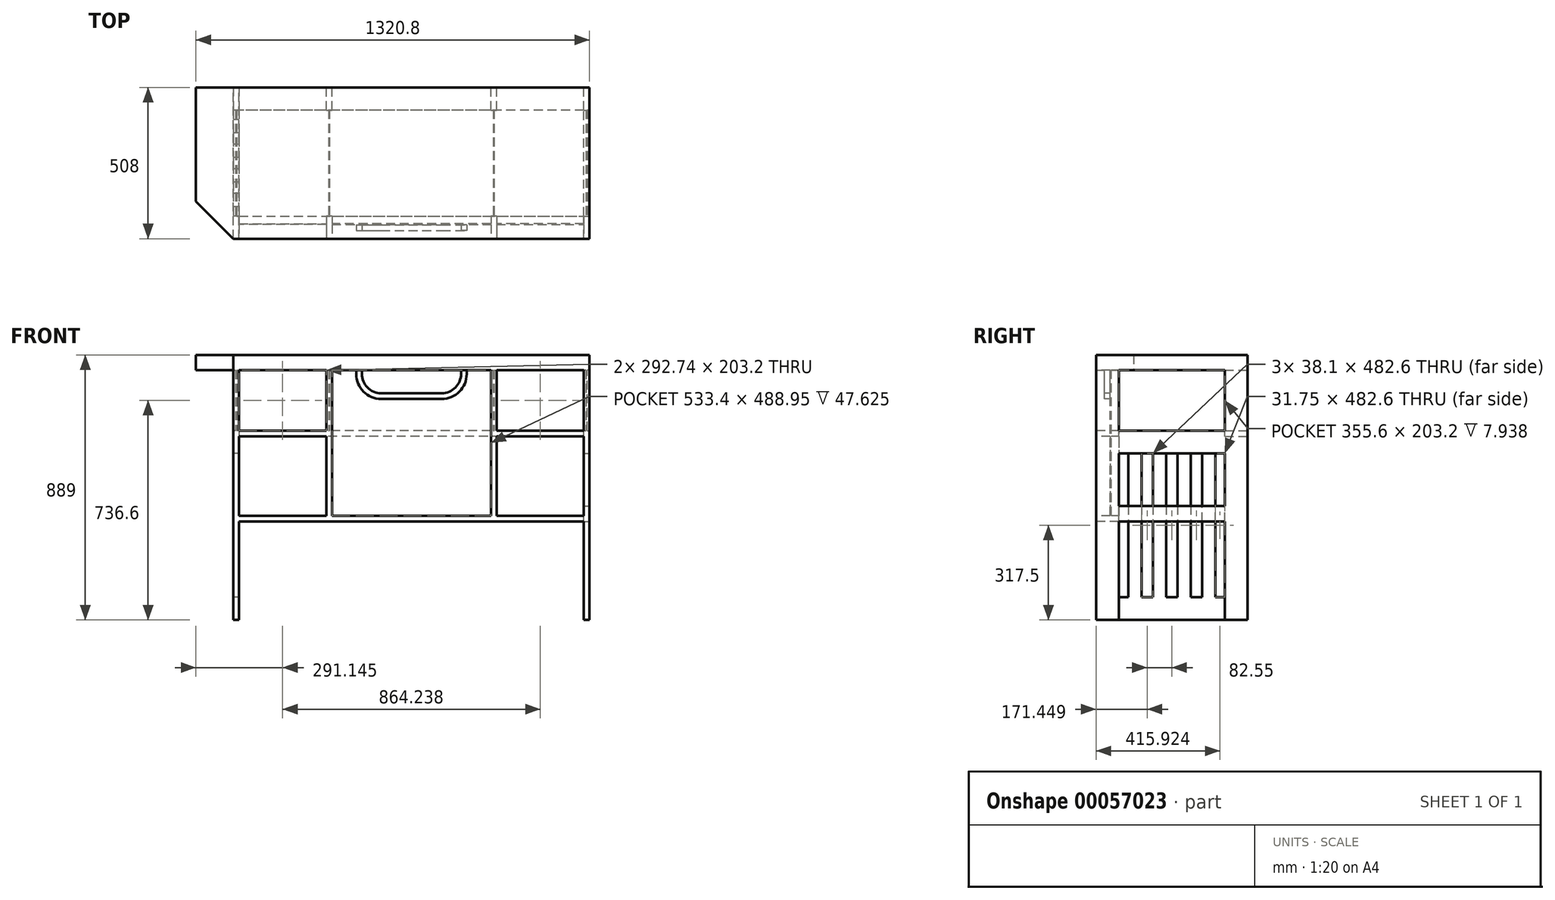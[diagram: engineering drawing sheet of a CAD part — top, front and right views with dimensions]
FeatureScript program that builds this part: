
annotation { "Feature Type Name" : "Feature", "Feature Type Description" : "" }
export const myFeature = defineFeature(function(context is Context, id is Id, definition is map)
    precondition{}
    {
        {
            var Q0;
            Q0=qCreatedBy(makeId("Top.planeOp"),FACE);
            var sketch = newSketch(context, id + "F0", { "sketchPlane" : qUnion([Q0])});
            skLineSegment(sketch, "E0", {"start": v(-703.39, 48.8) * mm, "end": v(617.41, 48.8) * mm});
            skLineSegment(sketch, "E1", {"start": v(617.41, 48.8) * mm, "end": v(617.41, -459.2) * mm});
            skLineSegment(sketch, "E2", {"start": v(617.41, -459.2) * mm, "end": v(-577.66, -459.2) * mm});
            skLineSegment(sketch, "E3", {"start": v(-577.66, -459.2) * mm, "end": v(-703.39, -333.48) * mm});
            skLineSegment(sketch, "E4", {"start": v(-703.39, -333.48) * mm, "end": v(-703.39, 48.8) * mm});
            skSolve(sketch);
        }
        {
            var Q0;
            Q0 = qSketchRegion(id + "F0", true);
            extrude(context, id + "F1", {"entities" : qUnion([Q0]), "depth" : 50.8 * mm});
        }
        {
            var Q0;
            Q0=makeQuery(id+"F1.opExtrude","CAP_FACE",FACE,{"disambiguationData":[OSD([sQuery(id+"F0.wireOp",EDGE,"E0"),sQuery(id+"F0.wireOp",EDGE,"E1"),sQuery(id+"F0.wireOp",EDGE,"E2"),sQuery(id+"F0.wireOp",EDGE,"E3"),sQuery(id+"F0.wireOp",EDGE,"E4")])],"isStart":true});
            var sketch = newSketch(context, id + "F2", { "sketchPlane" : qUnion([Q0])});
            skLineSegment(sketch, "E5.bottom", {"start": v(617.41, 459.2) * mm, "end": v(598.36, 459.2) * mm});
            skLineSegment(sketch, "E5.top", {"start": v(617.41, 383) * mm, "end": v(598.36, 383) * mm});
            skLineSegment(sketch, "E5.left", {"start": v(617.41, 459.2) * mm, "end": v(617.41, 383) * mm});
            skLineSegment(sketch, "E5.right", {"start": v(598.36, 459.2) * mm, "end": v(598.36, 383) * mm});
            skLineSegment(sketch, "E6.bottom", {"start": v(617.41, -48.8) * mm, "end": v(598.36, -48.8) * mm});
            skLineSegment(sketch, "E6.top", {"start": v(617.41, 27.4) * mm, "end": v(598.36, 27.4) * mm});
            skLineSegment(sketch, "E6.left", {"start": v(617.41, -48.8) * mm, "end": v(617.41, 27.4) * mm});
            skLineSegment(sketch, "E6.right", {"start": v(598.36, -48.8) * mm, "end": v(598.36, 27.4) * mm});
            skLineSegment(sketch, "E7.bottom", {"start": v(-577.66, 459.2) * mm, "end": v(-558.61, 459.2) * mm});
            skLineSegment(sketch, "E7.top", {"start": v(-577.66, 383) * mm, "end": v(-558.61, 383) * mm});
            skLineSegment(sketch, "E7.left", {"start": v(-577.66, 459.2) * mm, "end": v(-577.66, 383) * mm});
            skLineSegment(sketch, "E7.right", {"start": v(-558.61, 459.2) * mm, "end": v(-558.61, 383) * mm});
            skLineSegment(sketch, "E8.bottom", {"start": v(-577.66, -48.8) * mm, "end": v(-558.61, -48.8) * mm});
            skLineSegment(sketch, "E8.top", {"start": v(-577.66, 27.4) * mm, "end": v(-558.61, 27.4) * mm});
            skLineSegment(sketch, "E8.left", {"start": v(-577.66, -48.8) * mm, "end": v(-577.66, 27.4) * mm});
            skLineSegment(sketch, "E8.right", {"start": v(-558.61, -48.8) * mm, "end": v(-558.61, 27.4) * mm});
            skSolve(sketch);
        }
        {
            var Q0;
            Q0 = qSketchRegion(id + "F2", true);
            extrude(context, id + "F3", {"entities" : qUnion([Q0]), "operationType" : NewBodyOperationType.ADD, "depth" : 838.2 * mm});
        }
        {
            var Q0;
            Q0=makeQuery(id+"F3.opExtrude","SWEPT_FACE",FACE,{"disambiguationData":[OSD([sQuery(id+"F2.wireOp",EDGE,"E8.left")])]});
            var sketch = newSketch(context, id + "F4", { "sketchPlane" : qUnion([Q0])});
            skLineSegment(sketch, "E9.bottom", {"start": v(27.4, -203.2) * mm, "end": v(383, -203.2) * mm});
            skLineSegment(sketch, "E9.top", {"start": v(27.4, -279.4) * mm, "end": v(383, -279.4) * mm});
            skLineSegment(sketch, "E9.left", {"start": v(27.4, -203.2) * mm, "end": v(27.4, -279.4) * mm});
            skLineSegment(sketch, "E9.right", {"start": v(383, -203.2) * mm, "end": v(383, -279.4) * mm});
            skLineSegment(sketch, "E10.bottom", {"start": v(27.4, -838.2) * mm, "end": v(383, -838.2) * mm});
            skLineSegment(sketch, "E10.top", {"start": v(27.4, -762) * mm, "end": v(383, -762) * mm});
            skLineSegment(sketch, "E10.left", {"start": v(27.4, -838.2) * mm, "end": v(27.4, -762) * mm});
            skLineSegment(sketch, "E10.right", {"start": v(383, -838.2) * mm, "end": v(383, -762) * mm});
            skSolve(sketch);
        }
        {
            var Q0;
            Q0 = qSketchRegion(id + "F4", true);
            extrude(context, id + "F5", {"entities" : qUnion([Q0]), "operationType" : NewBodyOperationType.ADD, "oppositeDirection" : true, "depth" : 19.05 * mm});
        }
        {
            var Q0;
            Q0=makeQuery(id+"F5.boolean.opBoolean","MERGE",FACE,{"derivedFrom":[makeQuery(id+"F3.opExtrude","SWEPT_FACE",FACE,{"disambiguationData":[OSD([sQuery(id+"F2.wireOp",EDGE,"E7.left")])]}),makeQuery(id+"F3.opExtrude","SWEPT_FACE",FACE,{"disambiguationData":[OSD([sQuery(id+"F2.wireOp",EDGE,"E8.left")])]}),makeQuery(id+"F5.opExtrude","CAP_FACE",FACE,{"disambiguationData":[OSD([sQuery(id+"F4.wireOp",EDGE,"E9.bottom"),sQuery(id+"F4.wireOp",EDGE,"E9.top"),sQuery(id+"F4.wireOp",EDGE,"E9.left"),sQuery(id+"F4.wireOp",EDGE,"E9.right")])],"isStart":true}),makeQuery(id+"F5.opExtrude","CAP_FACE",FACE,{"disambiguationData":[OSD([sQuery(id+"F4.wireOp",EDGE,"E10.bottom"),sQuery(id+"F4.wireOp",EDGE,"E10.top"),sQuery(id+"F4.wireOp",EDGE,"E10.left"),sQuery(id+"F4.wireOp",EDGE,"E10.right")])],"isStart":true})]});
            var sketch = newSketch(context, id + "F6", { "sketchPlane" : qUnion([Q0])});
            skLineSegment(sketch, "E11.bottom", {"start": v(59.15, -762) * mm, "end": v(103.6, -762) * mm});
            skLineSegment(sketch, "E11.top", {"start": v(59.15, -279.4) * mm, "end": v(103.6, -279.4) * mm});
            skLineSegment(sketch, "E11.left", {"start": v(59.15, -762) * mm, "end": v(59.15, -279.4) * mm});
            skLineSegment(sketch, "E11.right", {"start": v(103.6, -762) * mm, "end": v(103.6, -279.4) * mm});
            skLineSegment(sketch, "E12.top", {"start": v(141.7, -762) * mm, "end": v(186.15, -762) * mm});
            skLineSegment(sketch, "E12.left", {"start": v(141.7, -279.4) * mm, "end": v(141.7, -762) * mm});
            skLineSegment(sketch, "E12.right", {"start": v(186.15, -279.4) * mm, "end": v(186.15, -762) * mm});
            skLineSegment(sketch, "E13.bottom", {"start": v(224.25, -279.4) * mm, "end": v(268.7, -279.4) * mm});
            skLineSegment(sketch, "E13.top", {"start": v(224.25, -762) * mm, "end": v(268.7, -762) * mm});
            skLineSegment(sketch, "E13.left", {"start": v(224.25, -279.4) * mm, "end": v(224.25, -762) * mm});
            skLineSegment(sketch, "E13.right", {"start": v(268.7, -279.4) * mm, "end": v(268.7, -762) * mm});
            skLineSegment(sketch, "E14.bottom", {"start": v(306.8, -279.4) * mm, "end": v(351.25, -279.4) * mm});
            skLineSegment(sketch, "E14.top", {"start": v(306.8, -762) * mm, "end": v(351.25, -762) * mm});
            skLineSegment(sketch, "E14.left", {"start": v(306.8, -279.4) * mm, "end": v(306.8, -762) * mm});
            skLineSegment(sketch, "E14.right", {"start": v(351.25, -279.4) * mm, "end": v(351.25, -762) * mm});
            skLineSegment(sketch, "E15", {"start": v(103.6, -279.4) * mm, "end": v(141.7, -279.4) * mm, "construction": true});
            skLineSegment(sketch, "E16", {"start": v(141.7, -279.4) * mm, "end": v(186.15, -279.4) * mm});
            skSolve(sketch);
        }
        {
            var Q0;
            Q0 = qSketchRegion(id + "F6", true);
            var Q1;
            Q1=makeQuery(id+"F5.boolean.opBoolean","MERGE",FACE,{"derivedFrom":[makeQuery(id+"F3.opExtrude","SWEPT_FACE",FACE,{"disambiguationData":[OSD([sQuery(id+"F2.wireOp",EDGE,"E7.right")])]}),makeQuery(id+"F3.opExtrude","SWEPT_FACE",FACE,{"disambiguationData":[OSD([sQuery(id+"F2.wireOp",EDGE,"E8.right")])]}),makeQuery(id+"F5.opExtrude","CAP_FACE",FACE,{"disambiguationData":[OSD([sQuery(id+"F4.wireOp",EDGE,"E9.bottom"),sQuery(id+"F4.wireOp",EDGE,"E9.top"),sQuery(id+"F4.wireOp",EDGE,"E9.left"),sQuery(id+"F4.wireOp",EDGE,"E9.right")])],"isStart":false}),makeQuery(id+"F5.opExtrude","CAP_FACE",FACE,{"disambiguationData":[OSD([sQuery(id+"F4.wireOp",EDGE,"E10.bottom"),sQuery(id+"F4.wireOp",EDGE,"E10.top"),sQuery(id+"F4.wireOp",EDGE,"E10.left"),sQuery(id+"F4.wireOp",EDGE,"E10.right")])],"isStart":false})]});
            extrude(context, id + "F7", {"entities" : qUnion([Q0]), "operationType" : NewBodyOperationType.ADD, "endBound" : BoundingType.UP_TO_SURFACE, "oppositeDirection" : true, "endBoundEntityFace" : qUnion([Q1]), "depth" : 25.4 * mm});
        }
        {
            var Q0;
            Q0=makeQuery(id+"F3.boolean.opBoolean","MERGE",FACE,{"derivedFrom":[makeQuery(id+"F1.opExtrude","SWEPT_FACE",FACE,{"disambiguationData":[OSD([sQuery(id+"F0.wireOp",EDGE,"E2")])]}),makeQuery(id+"F3.opExtrude","SWEPT_FACE",FACE,{"disambiguationData":[OSD([sQuery(id+"F2.wireOp",EDGE,"E5.bottom")])]}),makeQuery(id+"F3.opExtrude","SWEPT_FACE",FACE,{"disambiguationData":[OSD([sQuery(id+"F2.wireOp",EDGE,"E7.bottom")])]})]});
            var sketch = newSketch(context, id + "F8", { "sketchPlane" : qUnion([Q0])});
            skLineSegment(sketch, "E17.bottom", {"start": v(-265.88, 0) * mm, "end": v(-246.83, 0) * mm});
            skLineSegment(sketch, "E17.top", {"start": v(-265.88, -222.25) * mm, "end": v(-246.83, -222.25) * mm});
            skLineSegment(sketch, "E17.left", {"start": v(-265.88, 0) * mm, "end": v(-265.88, -222.25) * mm});
            skLineSegment(sketch, "E17.right", {"start": v(-246.83, 0) * mm, "end": v(-246.83, -222.25) * mm});
            skLineSegment(sketch, "E18.bottom", {"start": v(286.57, 0) * mm, "end": v(305.62, 0) * mm});
            skLineSegment(sketch, "E18.top", {"start": v(286.57, -222.25) * mm, "end": v(305.62, -222.25) * mm});
            skLineSegment(sketch, "E18.left", {"start": v(286.57, 0) * mm, "end": v(286.57, -222.25) * mm});
            skLineSegment(sketch, "E18.right", {"start": v(305.62, 0) * mm, "end": v(305.62, -222.25) * mm});
            skLineSegment(sketch, "E19", {"start": v(-265.88, 0) * mm, "end": v(-558.61, 0) * mm});
            skLineSegment(sketch, "E20", {"start": v(305.62, 0) * mm, "end": v(598.36, 0) * mm});
            skLineSegment(sketch, "E21.bottom", {"start": v(-265.88, -222.25) * mm, "end": v(-558.61, -222.25) * mm});
            skLineSegment(sketch, "E21.top", {"start": v(-265.88, -203.2) * mm, "end": v(-558.61, -203.2) * mm});
            skLineSegment(sketch, "E21.left", {"start": v(-265.88, -222.25) * mm, "end": v(-265.88, -203.2) * mm});
            skLineSegment(sketch, "E21.right", {"start": v(-558.61, -222.25) * mm, "end": v(-558.61, -203.2) * mm});
            skLineSegment(sketch, "E22.bottom", {"start": v(305.62, -222.25) * mm, "end": v(598.36, -222.25) * mm});
            skLineSegment(sketch, "E22.top", {"start": v(305.62, -203.2) * mm, "end": v(598.36, -203.2) * mm});
            skLineSegment(sketch, "E22.left", {"start": v(305.62, -222.25) * mm, "end": v(305.62, -203.2) * mm});
            skLineSegment(sketch, "E22.right", {"start": v(598.36, -222.25) * mm, "end": v(598.36, -203.2) * mm});
            skSolve(sketch);
        }
        {
            var Q0;
            Q0=makeQuery(id+"F7.boolean.opBoolean","MERGE",FACE,{"derivedFrom":[makeQuery(id+"F5.boolean.opBoolean","MERGE",FACE,{"derivedFrom":[makeQuery(id+"F3.opExtrude","SWEPT_FACE",FACE,{"disambiguationData":[OSD([sQuery(id+"F2.wireOp",EDGE,"E7.right")])]}),makeQuery(id+"F3.opExtrude","SWEPT_FACE",FACE,{"disambiguationData":[OSD([sQuery(id+"F2.wireOp",EDGE,"E8.right")])]}),makeQuery(id+"F5.opExtrude","CAP_FACE",FACE,{"disambiguationData":[OSD([sQuery(id+"F4.wireOp",EDGE,"E9.bottom"),sQuery(id+"F4.wireOp",EDGE,"E9.top"),sQuery(id+"F4.wireOp",EDGE,"E9.left"),sQuery(id+"F4.wireOp",EDGE,"E9.right")])],"isStart":false}),makeQuery(id+"F5.opExtrude","CAP_FACE",FACE,{"disambiguationData":[OSD([sQuery(id+"F4.wireOp",EDGE,"E10.bottom"),sQuery(id+"F4.wireOp",EDGE,"E10.top"),sQuery(id+"F4.wireOp",EDGE,"E10.left"),sQuery(id+"F4.wireOp",EDGE,"E10.right")])],"isStart":false})]}),makeQuery(id+"F7.opExtrude","CAP_FACE",FACE,{"disambiguationData":[OSD([sQuery(id+"F6.wireOp",EDGE,"E11.bottom"),sQuery(id+"F6.wireOp",EDGE,"E11.top"),sQuery(id+"F6.wireOp",EDGE,"E11.left"),sQuery(id+"F6.wireOp",EDGE,"E11.right")])],"isStart":false}),makeQuery(id+"F7.opExtrude","CAP_FACE",FACE,{"disambiguationData":[OSD([sQuery(id+"F6.wireOp",EDGE,"E12.top"),sQuery(id+"F6.wireOp",EDGE,"E12.left"),sQuery(id+"F6.wireOp",EDGE,"E12.right"),sQuery(id+"F6.wireOp",EDGE,"E16")])],"isStart":false}),makeQuery(id+"F7.opExtrude","CAP_FACE",FACE,{"disambiguationData":[OSD([sQuery(id+"F6.wireOp",EDGE,"E13.bottom"),sQuery(id+"F6.wireOp",EDGE,"E13.top"),sQuery(id+"F6.wireOp",EDGE,"E13.left"),sQuery(id+"F6.wireOp",EDGE,"E13.right")])],"isStart":false}),makeQuery(id+"F7.opExtrude","CAP_FACE",FACE,{"disambiguationData":[OSD([sQuery(id+"F6.wireOp",EDGE,"E14.bottom"),sQuery(id+"F6.wireOp",EDGE,"E14.top"),sQuery(id+"F6.wireOp",EDGE,"E14.left"),sQuery(id+"F6.wireOp",EDGE,"E14.right")])],"isStart":false})]});
            var sketch = newSketch(context, id + "F9", { "sketchPlane" : qUnion([Q0])});
            skLineSegment(sketch, "E23.bottom", {"start": v(-27.4, -203.2) * mm, "end": v(48.8, -203.2) * mm});
            skLineSegment(sketch, "E23.top", {"start": v(-27.4, -222.25) * mm, "end": v(48.8, -222.25) * mm});
            skLineSegment(sketch, "E23.left", {"start": v(-27.4, -203.2) * mm, "end": v(-27.4, -222.25) * mm});
            skLineSegment(sketch, "E23.right", {"start": v(48.8, -203.2) * mm, "end": v(48.8, -222.25) * mm});
            skSolve(sketch);
        }
        {
            var Q0;
            Q0 = qSketchRegion(id + "F9", true);
            var Q1;
            Q1=makeQuery(id+"F3.opExtrude","SWEPT_FACE",FACE,{"disambiguationData":[OSD([sQuery(id+"F2.wireOp",EDGE,"E5.right")])]});
            extrude(context, id + "F10", {"entities" : qUnion([Q0]), "operationType" : NewBodyOperationType.ADD, "endBound" : BoundingType.UP_TO_SURFACE, "endBoundEntityFace" : qUnion([Q1]), "depth" : 25.4 * mm});
        }
        {
            var Q0;
            Q0 = qSketchRegion(id + "F8", true);
            extrude(context, id + "F11", {"entities" : qUnion([Q0]), "operationType" : NewBodyOperationType.ADD, "oppositeDirection" : true, "depth" : 76.2 * mm});
        }
        {
            var Q0;
            Q0=makeQuery(id+"F10.boolean.opBoolean","MERGE",FACE,{"derivedFrom":[makeQuery(id+"F3.boolean.opBoolean","MERGE",FACE,{"derivedFrom":[makeQuery(id+"F1.opExtrude","SWEPT_FACE",FACE,{"disambiguationData":[OSD([sQuery(id+"F0.wireOp",EDGE,"E0")])]}),makeQuery(id+"F3.opExtrude","SWEPT_FACE",FACE,{"disambiguationData":[OSD([sQuery(id+"F2.wireOp",EDGE,"E6.bottom")])]}),makeQuery(id+"F3.opExtrude","SWEPT_FACE",FACE,{"disambiguationData":[OSD([sQuery(id+"F2.wireOp",EDGE,"E8.bottom")])]})]}),makeQuery(id+"F10.opExtrude","SWEPT_FACE",FACE,{"disambiguationData":[OSD([sQuery(id+"F9.wireOp",EDGE,"E23.right")])]})]});
            var sketch = newSketch(context, id + "F12", { "sketchPlane" : qUnion([Q0])});
            skLineSegment(sketch, "E24.bottom", {"start": v(-305.62, 0) * mm, "end": v(-286.57, 0) * mm});
            skLineSegment(sketch, "E24.top", {"start": v(-305.62, -203.2) * mm, "end": v(-286.57, -203.2) * mm});
            skLineSegment(sketch, "E24.left", {"start": v(-305.62, 0) * mm, "end": v(-305.62, -203.2) * mm});
            skLineSegment(sketch, "E24.right", {"start": v(-286.57, 0) * mm, "end": v(-286.57, -203.2) * mm});
            skLineSegment(sketch, "E25.bottom", {"start": v(246.83, 0) * mm, "end": v(265.88, 0) * mm});
            skLineSegment(sketch, "E25.top", {"start": v(246.83, -203.2) * mm, "end": v(265.88, -203.2) * mm});
            skLineSegment(sketch, "E25.left", {"start": v(246.83, 0) * mm, "end": v(246.83, -203.2) * mm});
            skLineSegment(sketch, "E25.right", {"start": v(265.88, 0) * mm, "end": v(265.88, -203.2) * mm});
            skSolve(sketch);
        }
        {
            var Q0;
            Q0 = qSketchRegion(id + "F12", true);
            extrude(context, id + "F13", {"entities" : qUnion([Q0]), "operationType" : NewBodyOperationType.ADD, "oppositeDirection" : true, "depth" : 76.2 * mm});
        }
        {
            var Q0;
            Q0=makeQuery(id+"F11.boolean.opBoolean","MERGE",FACE,{"derivedFrom":[makeQuery(id+"F3.boolean.opBoolean","MERGE",FACE,{"derivedFrom":[makeQuery(id+"F1.opExtrude","SWEPT_FACE",FACE,{"disambiguationData":[OSD([sQuery(id+"F0.wireOp",EDGE,"E2")])]}),makeQuery(id+"F3.opExtrude","SWEPT_FACE",FACE,{"disambiguationData":[OSD([sQuery(id+"F2.wireOp",EDGE,"E5.bottom")])]}),makeQuery(id+"F3.opExtrude","SWEPT_FACE",FACE,{"disambiguationData":[OSD([sQuery(id+"F2.wireOp",EDGE,"E7.bottom")])]})]}),makeQuery(id+"F11.opExtrude","CAP_FACE",FACE,{"disambiguationData":[OSD([sQuery(id+"F8.wireOp",EDGE,"E17.bottom"),sQuery(id+"F8.wireOp",EDGE,"E17.top"),sQuery(id+"F8.wireOp",EDGE,"E17.left"),sQuery(id+"F8.wireOp",EDGE,"E17.right"),sQuery(id+"F8.wireOp",EDGE,"E21.bottom"),sQuery(id+"F8.wireOp",EDGE,"E21.top"),sQuery(id+"F8.wireOp",EDGE,"E21.right")])],"isStart":true}),makeQuery(id+"F11.opExtrude","CAP_FACE",FACE,{"disambiguationData":[OSD([sQuery(id+"F8.wireOp",EDGE,"E18.bottom"),sQuery(id+"F8.wireOp",EDGE,"E18.top"),sQuery(id+"F8.wireOp",EDGE,"E18.left"),sQuery(id+"F8.wireOp",EDGE,"E18.right"),sQuery(id+"F8.wireOp",EDGE,"E22.bottom"),sQuery(id+"F8.wireOp",EDGE,"E22.top"),sQuery(id+"F8.wireOp",EDGE,"E22.right")])],"isStart":true})]});
            var sketch = newSketch(context, id + "F14", { "sketchPlane" : qUnion([Q0])});
            skLineSegment(sketch, "E26.bottom", {"start": v(-569.73, 0) * mm, "end": v(-566.55, 0) * mm});
            skLineSegment(sketch, "E26.top", {"start": v(-569.73, -203.2) * mm, "end": v(-566.55, -203.2) * mm});
            skLineSegment(sketch, "E26.left", {"start": v(-569.73, 0) * mm, "end": v(-569.73, -203.2) * mm});
            skLineSegment(sketch, "E26.right", {"start": v(-566.55, 0) * mm, "end": v(-566.55, -203.2) * mm});
            skLineSegment(sketch, "E27.bottom", {"start": v(-257.97, 0) * mm, "end": v(-254.8, 0) * mm});
            skLineSegment(sketch, "E27.top", {"start": v(-257.97, -203.2) * mm, "end": v(-254.8, -203.2) * mm});
            skLineSegment(sketch, "E27.left", {"start": v(-257.97, 0) * mm, "end": v(-257.97, -203.2) * mm});
            skLineSegment(sketch, "E27.right", {"start": v(-254.8, 0) * mm, "end": v(-254.8, -203.2) * mm});
            skLineSegment(sketch, "E28.bottom", {"start": v(294.51, 0) * mm, "end": v(297.69, 0) * mm});
            skLineSegment(sketch, "E28.top", {"start": v(294.51, -203.2) * mm, "end": v(297.69, -203.2) * mm});
            skLineSegment(sketch, "E28.left", {"start": v(294.51, 0) * mm, "end": v(294.51, -203.2) * mm});
            skLineSegment(sketch, "E28.right", {"start": v(297.69, 0) * mm, "end": v(297.69, -203.2) * mm});
            skLineSegment(sketch, "E29.bottom", {"start": v(606.3, 0) * mm, "end": v(609.48, 0) * mm});
            skLineSegment(sketch, "E29.top", {"start": v(606.3, -203.2) * mm, "end": v(609.48, -203.2) * mm});
            skLineSegment(sketch, "E29.left", {"start": v(606.3, 0) * mm, "end": v(606.3, -203.2) * mm});
            skLineSegment(sketch, "E29.right", {"start": v(609.48, 0) * mm, "end": v(609.48, -203.2) * mm});
            skSolve(sketch);
        }
        {
            var Q0;
            Q0 = qSketchRegion(id + "F14", true);
            var Q1;
            Q1=makeQuery(id+"F13.boolean.opBoolean","MERGE",FACE,{"derivedFrom":[makeQuery(id+"F10.boolean.opBoolean","MERGE",FACE,{"derivedFrom":[makeQuery(id+"F3.opExtrude","SWEPT_FACE",FACE,{"disambiguationData":[OSD([sQuery(id+"F2.wireOp",EDGE,"E6.top")])]}),makeQuery(id+"F10.opExtrude","SWEPT_FACE",FACE,{"disambiguationData":[OSD([sQuery(id+"F9.wireOp",EDGE,"E23.left")])]})]}),makeQuery(id+"F13.opExtrude","CAP_FACE",FACE,{"disambiguationData":[OSD([sQuery(id+"F12.wireOp",EDGE,"E24.bottom"),sQuery(id+"F12.wireOp",EDGE,"E24.top"),sQuery(id+"F12.wireOp",EDGE,"E24.left"),sQuery(id+"F12.wireOp",EDGE,"E24.right")])],"isStart":false}),makeQuery(id+"F13.opExtrude","CAP_FACE",FACE,{"disambiguationData":[OSD([sQuery(id+"F12.wireOp",EDGE,"E25.bottom"),sQuery(id+"F12.wireOp",EDGE,"E25.top"),sQuery(id+"F12.wireOp",EDGE,"E25.left"),sQuery(id+"F12.wireOp",EDGE,"E25.right")])],"isStart":false})]});
            extrude(context, id + "F15", {"entities" : qUnion([Q0]), "operationType" : NewBodyOperationType.ADD, "endBound" : BoundingType.UP_TO_SURFACE, "oppositeDirection" : true, "endBoundEntityFace" : qUnion([Q1]), "depth" : 25.4 * mm});
        }
        {
            var Q0;
            Q0=makeQuery(id+"F3.boolean.opBoolean","MERGE",FACE,{"derivedFrom":[makeQuery(id+"F1.opExtrude","SWEPT_FACE",FACE,{"disambiguationData":[OSD([sQuery(id+"F0.wireOp",EDGE,"E1")])]}),makeQuery(id+"F3.opExtrude","SWEPT_FACE",FACE,{"disambiguationData":[OSD([sQuery(id+"F2.wireOp",EDGE,"E5.left")])]}),makeQuery(id+"F3.opExtrude","SWEPT_FACE",FACE,{"disambiguationData":[OSD([sQuery(id+"F2.wireOp",EDGE,"E6.left")])]})]});
            var sketch = newSketch(context, id + "F16", { "sketchPlane" : qUnion([Q0])});
            skLineSegment(sketch, "E30.bottom", {"start": v(-383, -203.2) * mm, "end": v(-27.4, -203.2) * mm});
            skLineSegment(sketch, "E30.top", {"start": v(-383, -279.4) * mm, "end": v(-27.4, -279.4) * mm});
            skLineSegment(sketch, "E30.left", {"start": v(-383, -203.2) * mm, "end": v(-383, -279.4) * mm});
            skLineSegment(sketch, "E30.right", {"start": v(-27.4, -203.2) * mm, "end": v(-27.4, -279.4) * mm});
            skLineSegment(sketch, "E31.bottom", {"start": v(-27.4, -508) * mm, "end": v(-383, -508) * mm});
            skLineSegment(sketch, "E31.top", {"start": v(-27.4, -455.56) * mm, "end": v(-383, -455.56) * mm});
            skLineSegment(sketch, "E31.left", {"start": v(-27.4, -508) * mm, "end": v(-27.4, -455.56) * mm});
            skLineSegment(sketch, "E31.right", {"start": v(-383, -508) * mm, "end": v(-383, -455.56) * mm});
            skSolve(sketch);
        }
        {
            var Q0;
            Q0 = qSketchRegion(id + "F16", true);
            extrude(context, id + "F17", {"entities" : qUnion([Q0]), "operationType" : NewBodyOperationType.ADD, "oppositeDirection" : true, "depth" : 19.05 * mm});
        }
        {
            var Q0;
            Q0=makeQuery(id+"F11.boolean.opBoolean","MERGE",FACE,{"derivedFrom":[makeQuery(id+"F3.boolean.opBoolean","MERGE",FACE,{"derivedFrom":[makeQuery(id+"F1.opExtrude","SWEPT_FACE",FACE,{"disambiguationData":[OSD([sQuery(id+"F0.wireOp",EDGE,"E2")])]}),makeQuery(id+"F3.opExtrude","SWEPT_FACE",FACE,{"disambiguationData":[OSD([sQuery(id+"F2.wireOp",EDGE,"E5.bottom")])]}),makeQuery(id+"F3.opExtrude","SWEPT_FACE",FACE,{"disambiguationData":[OSD([sQuery(id+"F2.wireOp",EDGE,"E7.bottom")])]})]}),makeQuery(id+"F11.opExtrude","CAP_FACE",FACE,{"disambiguationData":[OSD([sQuery(id+"F8.wireOp",EDGE,"E17.bottom"),sQuery(id+"F8.wireOp",EDGE,"E17.top"),sQuery(id+"F8.wireOp",EDGE,"E17.left"),sQuery(id+"F8.wireOp",EDGE,"E17.right"),sQuery(id+"F8.wireOp",EDGE,"E21.bottom"),sQuery(id+"F8.wireOp",EDGE,"E21.top"),sQuery(id+"F8.wireOp",EDGE,"E21.right")])],"isStart":true}),makeQuery(id+"F11.opExtrude","CAP_FACE",FACE,{"disambiguationData":[OSD([sQuery(id+"F8.wireOp",EDGE,"E18.bottom"),sQuery(id+"F8.wireOp",EDGE,"E18.top"),sQuery(id+"F8.wireOp",EDGE,"E18.left"),sQuery(id+"F8.wireOp",EDGE,"E18.right"),sQuery(id+"F8.wireOp",EDGE,"E22.bottom"),sQuery(id+"F8.wireOp",EDGE,"E22.top"),sQuery(id+"F8.wireOp",EDGE,"E22.right")])],"isStart":true})]});
            cPlane(context, id + "F18", {"entities" : qUnion([Q0]), "cplaneType" : CPlaneType.OFFSET, "offset" : 50.8 * mm, "oppositeDirection" : true, "width" : 152.4 * mm, "height" : 152.4 * mm});
        }
        {
            var Q0;
            Q0=qCreatedBy(id+"F18.planeOp",FACE);
            var sketch = newSketch(context, id + "F19", { "sketchPlane" : qUnion([Q0])});
            skLineSegment(sketch, "E32", {"start": v(-145.23, 0) * mm, "end": v(-145.23, -12.7) * mm});
            skLineSegment(sketch, "E33", {"start": v(-81.73, -76.2) * mm, "end": v(121.47, -76.2) * mm});
            skLineSegment(sketch, "E34", {"start": v(184.97, -12.7) * mm, "end": v(184.97, 0) * mm});
            skPoint(sketch, "E35.visualSharp", {"position": v(-145.23, -76.2) * mm});
            skArc(sketch, "E35.filletArc", {"start": v(-145.23, -12.7) * mm, "mid": v(-126.63, -57.6) * mm, "end": v(-81.73, -76.2) * mm});
            skPoint(sketch, "E36.visualSharp", {"position": v(184.97, -76.2) * mm});
            skArc(sketch, "E36.filletArc", {"start": v(121.47, -76.2) * mm, "mid": v(166.38, -57.6) * mm, "end": v(184.97, -12.7) * mm});
            skSolve(sketch);
        }
        {
            var Q0;
            {var subQ15=sQuery(id+"F0.wireOp",EDGE,"E2");var subQ16=sQuery(id+"F8.wireOp",EDGE,"E17.right");var subQ23=sQuery(id+"F0.wireOp",EDGE,"E0");Q0=makeQuery(id+"F15.boolean.opBoolean","SPLIT",FACE,{"disambiguationData":[TD([makeQuery(id+"F11.opExtrude","SWEPT_FACE",FACE,{"disambiguationData":[OSD([subQ16])]})])],"derivedFrom":makeQuery(id+"F1.opExtrude","CAP_FACE",FACE,{"disambiguationData":[OSD([subQ23,sQuery(id+"F0.wireOp",EDGE,"E1"),subQ15,sQuery(id+"F0.wireOp",EDGE,"E3"),sQuery(id+"F0.wireOp",EDGE,"E4")])],"isStart":true})});}
            var sketch = newSketch(context, id + "F20", { "sketchPlane" : qUnion([Q0])});
            skLineSegment(sketch, "E37.bottom", {"start": v(-165.6, 412.27) * mm, "end": v(-146.55, 412.27) * mm});
            skLineSegment(sketch, "E37.top", {"start": v(-165.6, 431.32) * mm, "end": v(-146.55, 431.32) * mm});
            skLineSegment(sketch, "E37.left", {"start": v(-165.6, 412.27) * mm, "end": v(-165.6, 431.32) * mm});
            skLineSegment(sketch, "E37.right", {"start": v(-146.55, 412.27) * mm, "end": v(-146.55, 431.32) * mm});
            skSolve(sketch);
        }
        {
            var Q0;
            Q0 = qSketchRegion(id + "F20", true);
            var Q1;
            Q1 = qConstructionFilter(qBodyType(qCreatedBy(id + "F19" ,EDGE), BodyType.WIRE), ConstructionObject.NO);
            sweep(context, id + "F21", {"operationType" : NewBodyOperationType.ADD, "profiles" : qUnion([Q0]), "path" : qUnion([Q1])});
        }
        {
            var Q0;
            Q0=makeQuery(id+"F11.boolean.opBoolean","MERGE",FACE,{"derivedFrom":[makeQuery(id+"F3.boolean.opBoolean","MERGE",FACE,{"derivedFrom":[makeQuery(id+"F1.opExtrude","SWEPT_FACE",FACE,{"disambiguationData":[OSD([sQuery(id+"F0.wireOp",EDGE,"E2")])]}),makeQuery(id+"F3.opExtrude","SWEPT_FACE",FACE,{"disambiguationData":[OSD([sQuery(id+"F2.wireOp",EDGE,"E5.bottom")])]}),makeQuery(id+"F3.opExtrude","SWEPT_FACE",FACE,{"disambiguationData":[OSD([sQuery(id+"F2.wireOp",EDGE,"E7.bottom")])]})]}),makeQuery(id+"F11.opExtrude","CAP_FACE",FACE,{"disambiguationData":[OSD([sQuery(id+"F8.wireOp",EDGE,"E17.bottom"),sQuery(id+"F8.wireOp",EDGE,"E17.top"),sQuery(id+"F8.wireOp",EDGE,"E17.left"),sQuery(id+"F8.wireOp",EDGE,"E17.right"),sQuery(id+"F8.wireOp",EDGE,"E21.bottom"),sQuery(id+"F8.wireOp",EDGE,"E21.top"),sQuery(id+"F8.wireOp",EDGE,"E21.right")])],"isStart":true}),makeQuery(id+"F11.opExtrude","CAP_FACE",FACE,{"disambiguationData":[OSD([sQuery(id+"F8.wireOp",EDGE,"E18.bottom"),sQuery(id+"F8.wireOp",EDGE,"E18.top"),sQuery(id+"F8.wireOp",EDGE,"E18.left"),sQuery(id+"F8.wireOp",EDGE,"E18.right"),sQuery(id+"F8.wireOp",EDGE,"E22.bottom"),sQuery(id+"F8.wireOp",EDGE,"E22.top"),sQuery(id+"F8.wireOp",EDGE,"E22.right")])],"isStart":true})]});
            var sketch = newSketch(context, id + "F22", { "sketchPlane" : qUnion([Q0])});
            skLineSegment(sketch, "E38.bottom", {"start": v(-246.83, -222.25) * mm, "end": v(-265.88, -222.25) * mm});
            skLineSegment(sketch, "E38.top", {"start": v(-246.83, -508) * mm, "end": v(-265.88, -508) * mm});
            skLineSegment(sketch, "E38.left", {"start": v(-246.83, -222.25) * mm, "end": v(-246.83, -508) * mm});
            skLineSegment(sketch, "E38.right", {"start": v(-265.88, -222.25) * mm, "end": v(-265.88, -508) * mm});
            skLineSegment(sketch, "E39.bottom", {"start": v(-265.88, -508) * mm, "end": v(-558.61, -508) * mm});
            skLineSegment(sketch, "E39.top", {"start": v(-265.88, -488.95) * mm, "end": v(-558.61, -488.95) * mm});
            skLineSegment(sketch, "E39.left", {"start": v(-265.88, -508) * mm, "end": v(-265.88, -488.95) * mm});
            skLineSegment(sketch, "E39.right", {"start": v(-558.61, -508) * mm, "end": v(-558.61, -488.95) * mm});
            skLineSegment(sketch, "E40.bottom", {"start": v(286.57, -222.25) * mm, "end": v(305.62, -222.25) * mm});
            skLineSegment(sketch, "E40.top", {"start": v(286.57, -508) * mm, "end": v(305.62, -508) * mm});
            skLineSegment(sketch, "E40.left", {"start": v(286.57, -222.25) * mm, "end": v(286.57, -508) * mm});
            skLineSegment(sketch, "E40.right", {"start": v(305.62, -222.25) * mm, "end": v(305.62, -508) * mm});
            skLineSegment(sketch, "E41.bottom", {"start": v(305.62, -508) * mm, "end": v(598.36, -508) * mm});
            skLineSegment(sketch, "E41.top", {"start": v(305.62, -488.95) * mm, "end": v(598.36, -488.95) * mm});
            skLineSegment(sketch, "E41.left", {"start": v(305.62, -508) * mm, "end": v(305.62, -488.95) * mm});
            skLineSegment(sketch, "E41.right", {"start": v(598.36, -508) * mm, "end": v(598.36, -488.95) * mm});
            skLineSegment(sketch, "E42.bottom", {"start": v(-246.83, -508) * mm, "end": v(286.57, -508) * mm});
            skLineSegment(sketch, "E42.top", {"start": v(-246.83, -488.95) * mm, "end": v(286.57, -488.95) * mm});
            skLineSegment(sketch, "E42.left", {"start": v(-246.83, -508) * mm, "end": v(-246.83, -488.95) * mm});
            skLineSegment(sketch, "E42.right", {"start": v(286.57, -508) * mm, "end": v(286.57, -488.95) * mm});
            skSolve(sketch);
        }
        {
            var Q0;
            Q0 = qSketchRegion(id + "F22", true);
            extrude(context, id + "F23", {"entities" : qUnion([Q0]), "operationType" : NewBodyOperationType.ADD, "oppositeDirection" : true, "depth" : 76.2 * mm});
        }
        {
            var Q0;
            Q0=qCreatedBy(id+"F18.planeOp",FACE);
            var sketch = newSketch(context, id + "F24", { "sketchPlane" : qUnion([Q0])});
            skLineSegment(sketch, "E43", {"start": v(-558.61, -488.95) * mm, "end": v(-558.61, -222.25) * mm});
            skLineSegment(sketch, "E44", {"start": v(-558.61, -222.25) * mm, "end": v(-246.83, -222.25) * mm});
            skLineSegment(sketch, "E45", {"start": v(-246.83, -222.25) * mm, "end": v(-246.83, 0) * mm});
            skLineSegment(sketch, "E46", {"start": v(-246.83, 0) * mm, "end": v(286.57, 0) * mm});
            skLineSegment(sketch, "E47", {"start": v(286.57, 0) * mm, "end": v(286.57, -222.25) * mm});
            skLineSegment(sketch, "E48", {"start": v(286.57, -222.25) * mm, "end": v(598.36, -222.25) * mm});
            skLineSegment(sketch, "E49", {"start": v(598.36, -222.25) * mm, "end": v(598.36, -488.95) * mm});
            skLineSegment(sketch, "E50", {"start": v(598.36, -488.95) * mm, "end": v(-558.61, -488.95) * mm});
            skSolve(sketch);
        }
        {
            var Q0;
            Q0 = qSketchRegion(id + "F24", true);
            extrude(context, id + "F25", {"entities" : qUnion([Q0]), "operationType" : NewBodyOperationType.ADD, "depth" : 3.17 * mm});
        }
    });
